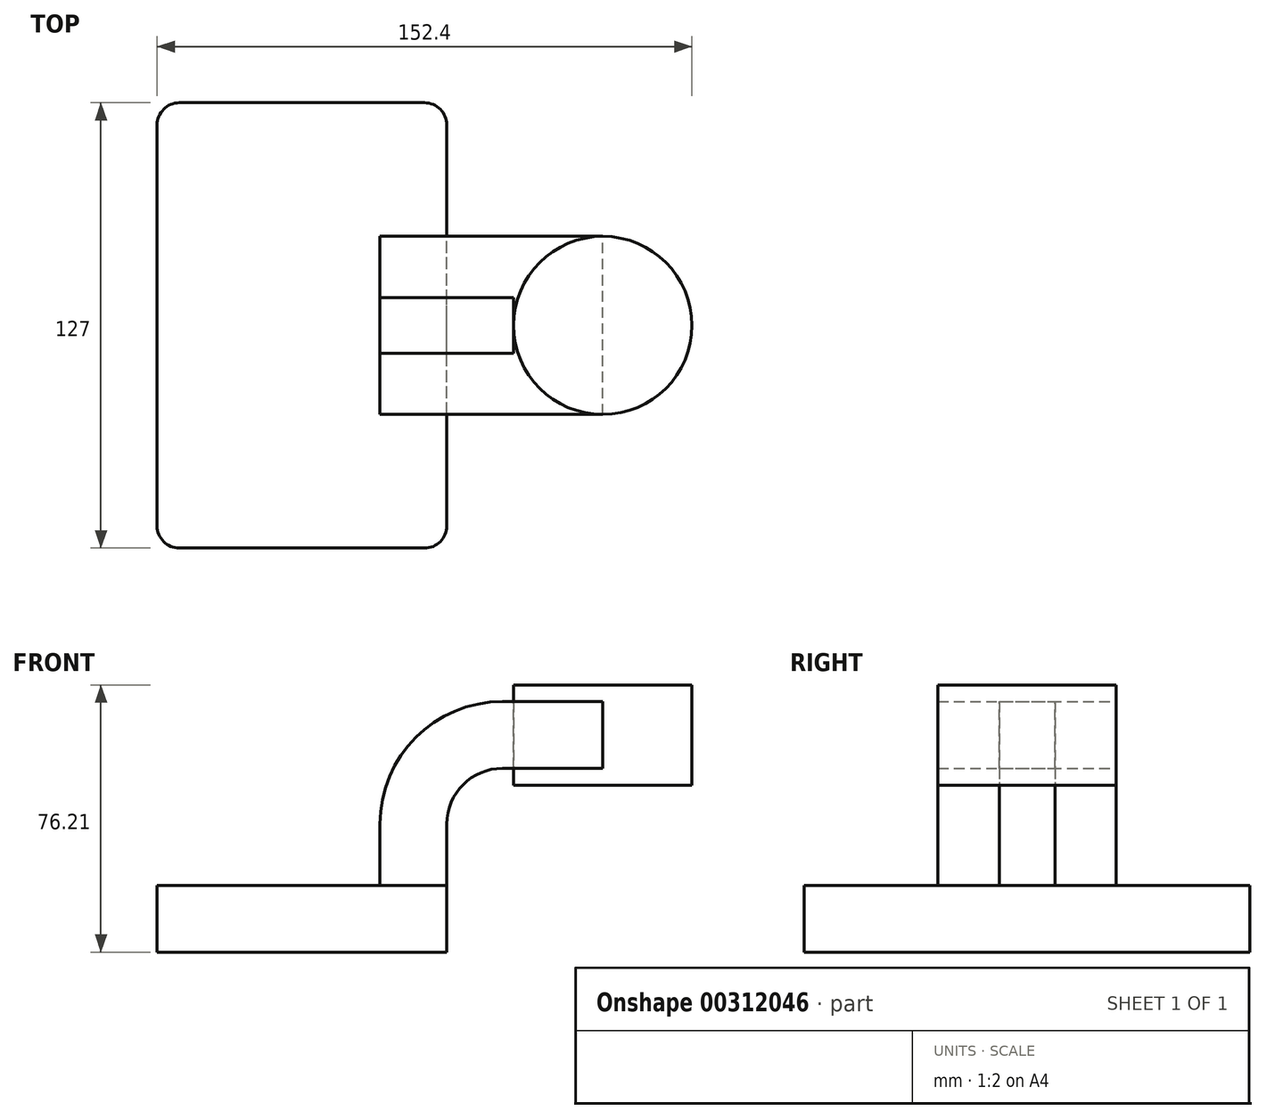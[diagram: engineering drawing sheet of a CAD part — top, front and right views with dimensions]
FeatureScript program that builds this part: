
annotation { "Feature Type Name" : "Feature", "Feature Type Description" : "" }
export const myFeature = defineFeature(function(context is Context, id is Id, definition is map)
    precondition{}
    {
        {
            var Q0;
            Q0=qCreatedBy(makeId("Front.planeOp"),FACE);
            var sketch = newSketch(context, id + "F0", { "sketchPlane" : qUnion([Q0])});
            skLineSegment(sketch, "E0.bottom", {"start": v(41.28, 9.52) * mm, "end": v(-41.28, 9.53) * mm});
            skLineSegment(sketch, "E0.top", {"start": v(41.28, -9.53) * mm, "end": v(-41.28, -9.52) * mm});
            skLineSegment(sketch, "E0.left", {"start": v(41.28, 9.52) * mm, "end": v(41.28, -9.53) * mm});
            skLineSegment(sketch, "E0.right", {"start": v(-41.28, 9.53) * mm, "end": v(-41.28, -9.52) * mm});
            skPoint(sketch, "E0.middle", {"position": v(0, 0) * mm});
            skLineSegment(sketch, "E1.bottom", {"start": v(60.33, 38.1) * mm, "end": v(111.12, 38.1) * mm});
            skLineSegment(sketch, "E1.top", {"start": v(60.32, 66.68) * mm, "end": v(111.12, 66.68) * mm});
            skLineSegment(sketch, "E1.left", {"start": v(60.33, 38.1) * mm, "end": v(60.32, 66.68) * mm});
            skLineSegment(sketch, "E1.right", {"start": v(111.12, 38.1) * mm, "end": v(111.12, 66.68) * mm});
            skPoint(sketch, "E1.middle", {"position": v(85.72, 52.39) * mm});
            skLineSegment(sketch, "E2", {"start": v(41.28, 9.52) * mm, "end": v(41.28, 27) * mm});
            skArc(sketch, "E3", {"start": v(41.28, 27) * mm, "mid": v(45.92, 38.23) * mm, "end": v(57.15, 42.88) * mm});
            skLineSegment(sketch, "E4", {"start": v(57.15, 42.88) * mm, "end": v(85.72, 42.88) * mm});
            skLineSegment(sketch, "E5.0", {"start": v(57.15, 61.93) * mm, "end": v(85.72, 61.93) * mm});
            skArc(sketch, "E5.1", {"start": v(22.23, 27) * mm, "mid": v(32.45, 51.7) * mm, "end": v(57.15, 61.93) * mm});
            skLineSegment(sketch, "E5.2", {"start": v(22.22, 9.52) * mm, "end": v(22.22, 27) * mm});
            skLineSegment(sketch, "E6", {"start": v(85.72, 38.1) * mm, "end": v(85.72, 66.68) * mm});
            skFitSpline(sketch, "E7", {"points": [v(-41.28, 9.53) * mm, v(57.15, 61.93) * mm], "startDerivative": vector(23.15, 83.52) * mm, "endDerivative": vector(102.3, -3.58) * mm});
            skSolve(sketch);
        }
        {
            var Q0;
            Q0=makeQuery(id+"F0.imprint","IMPRINT",FACE,{"disambiguationData":[TD([[makeQuery(id+"F0.imprint","IMPRINT",EDGE,{"derivedFrom":sQuery(id+"F0.wireOp",EDGE,"E0.top")}),-1.0]])]});
            extrude(context, id + "F1", {"entities" : qUnion([Q0]), "endBound" : BoundingType.SYMMETRIC, "depth" : 127 * mm});
        }
        {
            var Q0;
            {var subQ1=sQuery(id+"F0.wireOp",EDGE,"E2");Q0=makeQuery(id+"F0.imprint","IMPRINT",FACE,{"disambiguationData":[TD([[makeQuery(id+"F0.imprint","IMPRINT",EDGE,{"derivedFrom":subQ1}),1.0]])]});}
            var Q1;
            {var subQ0=sQuery(id+"F0.wireOp",EDGE,"E4");var subQ1=sQuery(id+"F0.wireOp",EDGE,"E1.left");var subQ2=makeQuery(id+"F0.imprint","INTERSECT",VERTEX,{"derivedFrom":[subQ1,subQ0]});Q1=makeQuery(id+"F0.imprint","IMPRINT",FACE,{"disambiguationData":[TD([[makeQuery(id+"F0.imprint","IMPRINT",EDGE,{"disambiguationData":[TD([[subQ2,-1.0]])],"derivedFrom":subQ1}),-1.0]])]});}
            extrude(context, id + "F2", {"entities" : qUnion([Q0, Q1]), "endBound" : BoundingType.SYMMETRIC, "depth" : 50.8 * mm});
        }
        {
            var Q0;
            Q0=makeQuery(id+"F0.imprint","IMPRINT",FACE,{"disambiguationData":[TD([[makeQuery(id+"F0.imprint","IMPRINT",EDGE,{"derivedFrom":sQuery(id+"F0.wireOp",EDGE,"E5.1")}),1.0]])]});
            extrude(context, id + "F3", {"entities" : qUnion([Q0]), "endBound" : BoundingType.SYMMETRIC, "depth" : 15.88 * mm});
        }
        {
            var Q0;
            {var subQ0=sQuery(id+"F0.wireOp",EDGE,"E1.right");Q0=makeQuery(id+"F0.imprint","IMPRINT",FACE,{"disambiguationData":[TD([[makeQuery(id+"F0.imprint","IMPRINT",EDGE,{"derivedFrom":subQ0}),1.0]])]});}
            var Q1;
            Q1=sQuery(id+"F0.wireOp",EDGE,"E6");
            revolve(context, id + "F4", {"entities" : qUnion([Q0]), "axis" : qUnion([Q1]), "revolveType" : RevolveType.FULL});
        }
        {
            var Q0;
            Q0=makeQuery(id+"F1.opExtrude","CAP_EDGE",EDGE,{"disambiguationData":[OSD([sQuery(id+"F0.wireOp",EDGE,"E0.right")])],"isStart":false});
            var Q1;
            Q1=makeQuery(id+"F1.opExtrude","CAP_EDGE",EDGE,{"disambiguationData":[OSD([sQuery(id+"F0.wireOp",EDGE,"E0.left")])],"isStart":false});
            var Q2;
            Q2=makeQuery(id+"F1.opExtrude","CAP_EDGE",EDGE,{"disambiguationData":[OSD([sQuery(id+"F0.wireOp",EDGE,"E0.right")])],"isStart":true});
            var Q3;
            Q3=makeQuery(id+"F1.opExtrude","CAP_EDGE",EDGE,{"disambiguationData":[OSD([sQuery(id+"F0.wireOp",EDGE,"E0.left")])],"isStart":true});
            fillet(context, id + "F5", {"entities" : qUnion([Q0, Q1, Q2, Q3]), "radius" : 6.35 * mm, "tangentPropagation" : true, "allowEdgeOverflow" : false});
        }
    });
